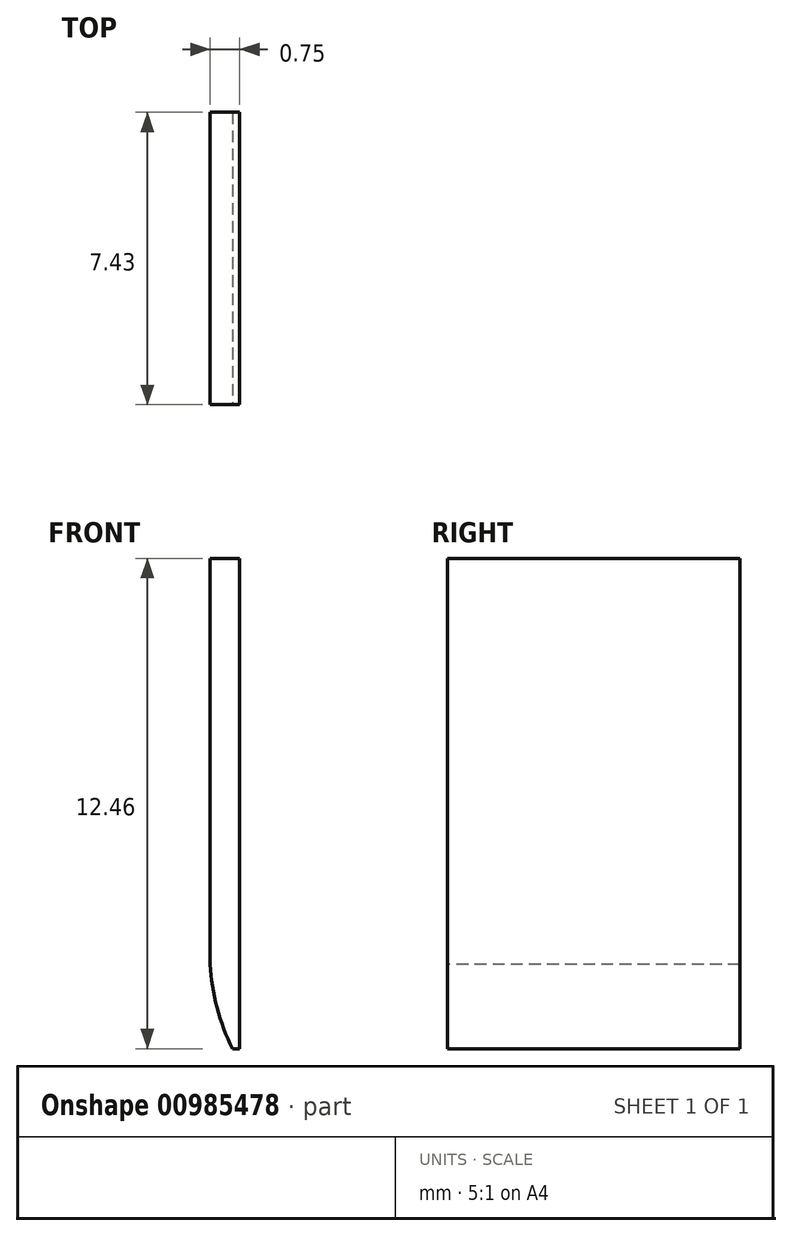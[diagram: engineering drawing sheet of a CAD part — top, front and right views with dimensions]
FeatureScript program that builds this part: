
annotation { "Feature Type Name" : "Feature", "Feature Type Description" : "" }
export const myFeature = defineFeature(function(context is Context, id is Id, definition is map)
    precondition{}
    {
        {
            var Q0;
            Q0=qCreatedBy(makeId("Right.planeOp"),FACE);
            var sketch = newSketch(context, id + "F0", { "sketchPlane" : qUnion([Q0])});
            skLineSegment(sketch, "E0.bottom", {"start": v(0.41, 0) * mm, "end": v(7.84, 0) * mm});
            skLineSegment(sketch, "E0.top", {"start": v(0.41, 12.46) * mm, "end": v(7.84, 12.46) * mm});
            skLineSegment(sketch, "E0.left", {"start": v(0.41, 0) * mm, "end": v(0.41, 12.46) * mm});
            skLineSegment(sketch, "E0.right", {"start": v(7.84, 0) * mm, "end": v(7.84, 12.46) * mm});
            skSolve(sketch);
        }
        {
            var Q0;
            Q0=qSketchRegion(id+"F0",true);
            extrude(context, id + "F1", {"entities" : qUnion([Q0]), "depth" : .75 * mm});
        }
        {
            var Q0;
            Q0=makeQuery(id+"F1.opExtrude","SWEPT_FACE",FACE,{"disambiguationData":[OSD([sQuery(id+"F0.wireOp",EDGE,"E0.left")])]});
            var sketch = newSketch(context, id + "F2", { "sketchPlane" : qUnion([Q0])});
            skArc(sketch, "E1", {"start": v(0, 2.15) * mm, "mid": v(0.17, 1.04) * mm, "end": v(0.57, 0) * mm});
            skLineSegment(sketch, "E2", {"start": v(0, 2.15) * mm, "end": v(0, 0) * mm});
            skLineSegment(sketch, "E3", {"start": v(0, 0) * mm, "end": v(0.57, 0) * mm});
            skSolve(sketch);
        }
        {
            var Q0;
            Q0=qSketchRegion(id+"F2",true);
            extrude(context, id + "F3", {"entities" : qUnion([Q0]), "operationType" : NewBodyOperationType.REMOVE, "endBound" : BoundingType.THROUGH_ALL, "oppositeDirection" : true, "depth" : 25 * mm});
        }
    });
